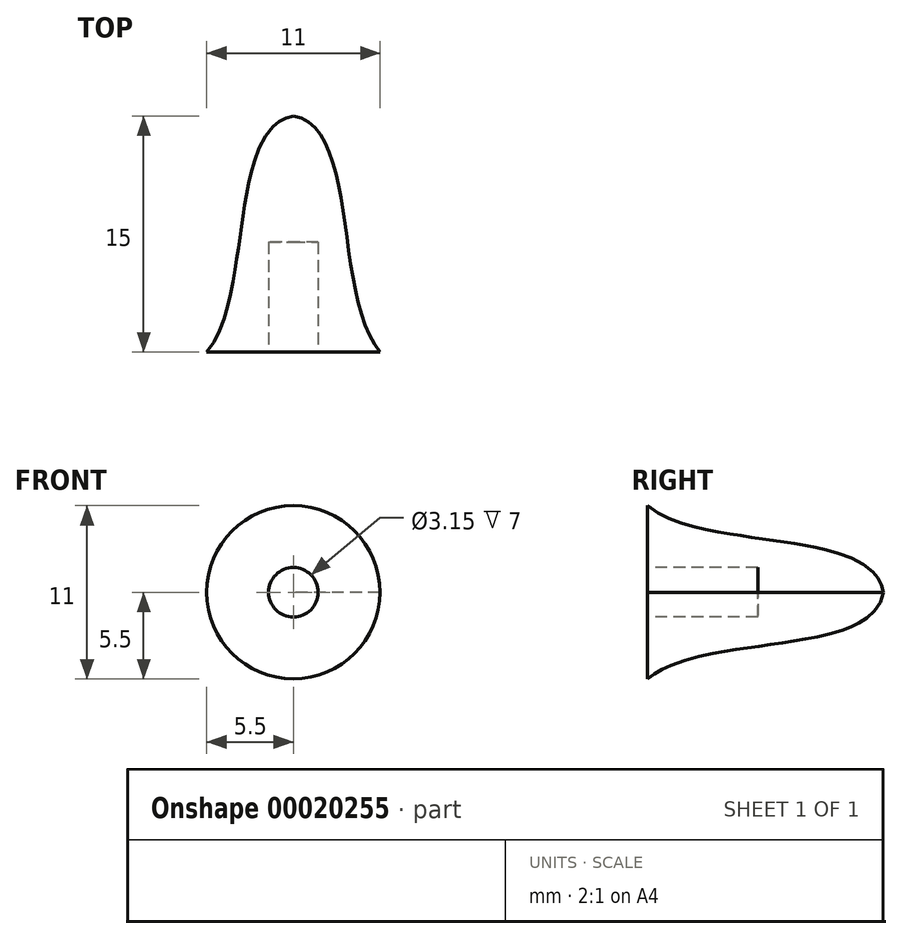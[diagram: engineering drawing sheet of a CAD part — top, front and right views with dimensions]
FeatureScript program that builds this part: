
annotation { "Feature Type Name" : "Feature", "Feature Type Description" : "" }
export const myFeature = defineFeature(function(context is Context, id is Id, definition is map)
    precondition{}
    {
        {
            var Q0;
            Q0=qCreatedBy(makeId("Top.planeOp"),FACE);
            var sketch = newSketch(context, id + "F0", { "sketchPlane" : qUnion([Q0])});
            skLineSegment(sketch, "E0.bottom", {"start": v(1.57, 0) * mm, "end": v(5.5, 0) * mm});
            skLineSegment(sketch, "E0.left", {"start": v(0, 7) * mm, "end": v(0, 15) * mm});
            skFitSpline(sketch, "E1", {"points": [v(5.5, 0) * mm, v(0, 15) * mm], "startDerivative": vector(-8.91, 10.74) * mm, "endDerivative": vector(-12.6, 2.05) * mm});
            skLineSegment(sketch, "E2.top", {"start": v(0, 7) * mm, "end": v(1.57, 7) * mm});
            skLineSegment(sketch, "E2.right", {"start": v(1.57, 0) * mm, "end": v(1.57, 7) * mm});
            skSolve(sketch);
        }
        {
            var Q0;
            Q0 = qSketchRegion(id + "F0", true);
            var Q1;
            Q1=sQuery(id+"F0.wireOp",EDGE,"E0.left");
            revolve(context, id + "F1", {"entities" : qUnion([Q0]), "axis" : qUnion([Q1]), "revolveType" : RevolveType.FULL});
        }
    });
